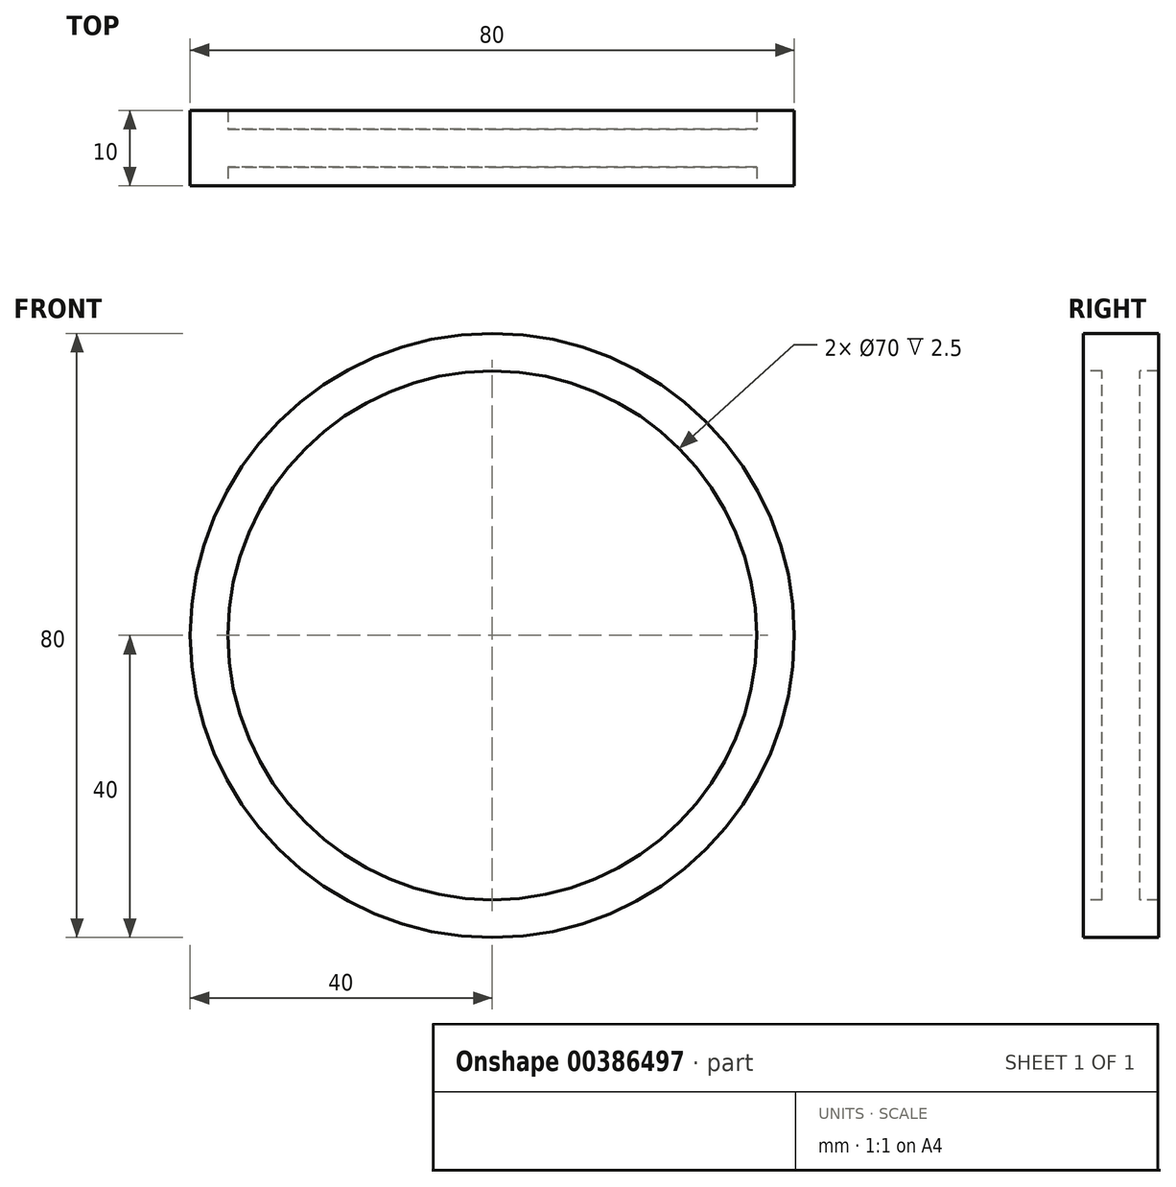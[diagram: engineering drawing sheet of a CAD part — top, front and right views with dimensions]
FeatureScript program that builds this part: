
annotation { "Feature Type Name" : "Feature", "Feature Type Description" : "" }
export const myFeature = defineFeature(function(context is Context, id is Id, definition is map)
    precondition{}
    {
        {
            var Q0;
            Q0=qCreatedBy(makeId("Top.planeOp"),FACE);
            var sketch = newSketch(context, id + "F0", { "sketchPlane" : qUnion([Q0])});
            skLineSegment(sketch, "E0.bottom", {"start": v(0, 0) * mm, "end": v(-35, 0) * mm});
            skLineSegment(sketch, "E0.top", {"start": v(0, 5) * mm, "end": v(-35, 5) * mm});
            skLineSegment(sketch, "E0.left", {"start": v(0, 0) * mm, "end": v(0, 5) * mm});
            skLineSegment(sketch, "E1.bottom", {"start": v(-35, 7.5) * mm, "end": v(-40, 7.5) * mm});
            skLineSegment(sketch, "E1.top", {"start": v(-35, -2.5) * mm, "end": v(-40, -2.5) * mm});
            skLineSegment(sketch, "E1.left", {"start": v(-35, 7.5) * mm, "end": v(-35, 5) * mm});
            skLineSegment(sketch, "E1.right", {"start": v(-40, 7.5) * mm, "end": v(-40, -2.5) * mm});
            skLineSegment(sketch, "E2.trimOffspring", {"start": v(-35, 0) * mm, "end": v(-35, -2.5) * mm});
            skSolve(sketch);
        }
        {
            var Q0;
            Q0=makeQuery(id+"F0.imprint","IMPRINT",FACE,{"disambiguationData":[TD([[makeQuery(id+"F0.imprint","IMPRINT",EDGE,{"derivedFrom":sQuery(id+"F0.wireOp",EDGE,"E0.bottom")}),-1.0]])]});
            var Q1;
            Q1=sQuery(id+"F0.wireOp",EDGE,"E0.top");
            var Q2;
            Q2=sQuery(id+"F0.wireOp",EDGE,"E1.right");
            var Q3;
            Q3=sQuery(id+"F0.wireOp",EDGE,"E0.bottom");
            var Q4;
            Q4=sQuery(id+"F0.wireOp",EDGE,"E1.top");
            var Q5;
            Q5=sQuery(id+"F0.wireOp",EDGE,"E1.bottom");
            var Q6;
            Q6=sQuery(id+"F0.wireOp",EDGE,"E0.left");
            var Q7;
            Q7=sQuery(id+"F0.wireOp",EDGE,"E1.left");
            var Q8;
            Q8=sQuery(id+"F0.wireOp",EDGE,"E2.trimOffspring");
            var Q9;
            Q9=sQuery(id+"F0.wireOp",EDGE,"E0.left");
            revolve(context, id + "F1", {"entities" : qUnion([Q0]), "surfaceEntities" : qUnion([Q1, Q2, Q3, Q4, Q5, Q6, Q7, Q8]), "axis" : qUnion([Q9]), "revolveType" : RevolveType.FULL});
        }
    });
